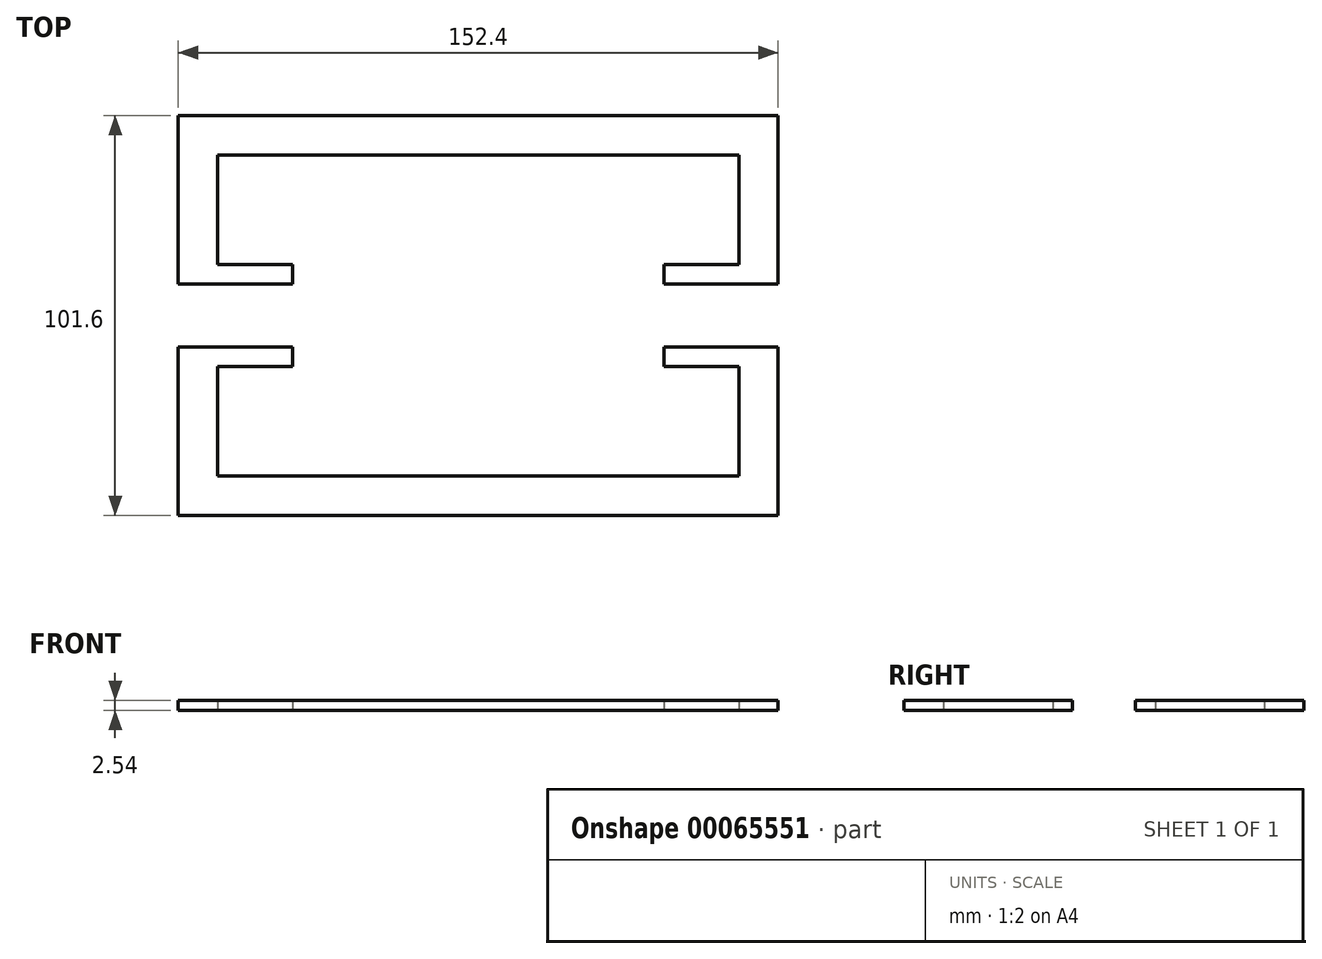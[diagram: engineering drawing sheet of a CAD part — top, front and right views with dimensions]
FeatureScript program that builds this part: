
annotation { "Feature Type Name" : "Feature", "Feature Type Description" : "" }
export const myFeature = defineFeature(function(context is Context, id is Id, definition is map)
    precondition{}
    {
        {
            var Q0;
            Q0=qCreatedBy(makeId("Top.planeOp"),FACE);
            var sketch = newSketch(context, id + "F0", { "sketchPlane" : qUnion([Q0])});
            skLineSegment(sketch, "E0", {"start": v(-76.2, 0) * mm, "end": v(76.2, 0) * mm});
            skLineSegment(sketch, "E1", {"start": v(76.2, 0) * mm, "end": v(76.2, 42.8) * mm});
            skLineSegment(sketch, "E2", {"start": v(-76.2, 0) * mm, "end": v(-76.2, 101.6) * mm});
            skLineSegment(sketch, "E3", {"start": v(76.2, 101.6) * mm, "end": v(-76.2, 101.6) * mm});
            skPoint(sketch, "E4", {"position": v(76.2, 50.8) * mm});
            skPoint(sketch, "E5", {"position": v(-76.2, 50.8) * mm});
            skPoint(sketch, "E6", {"position": v(0, 101.6) * mm});
            skPoint(sketch, "E7", {"position": v(-76.2, 58.8) * mm});
            skPoint(sketch, "E8", {"position": v(-76.2, 42.8) * mm});
            skLineSegment(sketch, "E9", {"start": v(-76.2, 58.8) * mm, "end": v(-76.2, 42.8) * mm});
            skLineSegment(sketch, "E10", {"start": v(-76.2, 58.8) * mm, "end": v(-47.2, 58.8) * mm});
            skLineSegment(sketch, "E11", {"start": v(-76.2, 42.8) * mm, "end": v(-47.2, 42.8) * mm});
            skLineSegment(sketch, "E12", {"start": v(-76.2, 37.8) * mm, "end": v(-47.2, 37.8) * mm});
            skLineSegment(sketch, "E13", {"start": v(-76.2, 63.8) * mm, "end": v(-47.2, 63.8) * mm});
            skLineSegment(sketch, "E14", {"start": v(-47.2, 63.8) * mm, "end": v(-47.2, 58.8) * mm});
            skLineSegment(sketch, "E15", {"start": v(-47.2, 42.8) * mm, "end": v(-47.2, 37.8) * mm});
            skLineSegment(sketch, "E16", {"start": v(-76.2, 63.8) * mm, "end": v(-76.2, 58.8) * mm});
            skLineSegment(sketch, "E17", {"start": v(-76.2, 42.8) * mm, "end": v(-76.2, 37.8) * mm});
            skPoint(sketch, "E18", {"position": v(76.2, 58.8) * mm});
            skPoint(sketch, "E19", {"position": v(76.2, 42.8) * mm});
            skLineSegment(sketch, "E20.trimOffspring", {"start": v(76.2, 58.8) * mm, "end": v(76.2, 101.6) * mm});
            skLineSegment(sketch, "E21", {"start": v(76.2, 42.8) * mm, "end": v(76.2, 58.8) * mm});
            skLineSegment(sketch, "E22", {"start": v(76.2, 42.8) * mm, "end": v(47.2, 42.8) * mm});
            skLineSegment(sketch, "E23", {"start": v(76.2, 37.8) * mm, "end": v(47.2, 37.8) * mm});
            skLineSegment(sketch, "E24", {"start": v(76.2, 58.8) * mm, "end": v(47.2, 58.8) * mm});
            skLineSegment(sketch, "E25", {"start": v(76.2, 63.8) * mm, "end": v(47.2, 63.8) * mm});
            skLineSegment(sketch, "E26", {"start": v(-66.2, 63.8) * mm, "end": v(-66.2, 91.6) * mm});
            skLineSegment(sketch, "E27", {"start": v(-66.2, 37.8) * mm, "end": v(-66.2, 10) * mm});
            skLineSegment(sketch, "E28", {"start": v(-66.2, 10) * mm, "end": v(66.2, 10) * mm});
            skLineSegment(sketch, "E29", {"start": v(66.2, 91.6) * mm, "end": v(66.2, 63.8) * mm});
            skLineSegment(sketch, "E30", {"start": v(66.2, 37.8) * mm, "end": v(66.2, 10) * mm});
            skLineSegment(sketch, "E31", {"start": v(-66.2, 91.6) * mm, "end": v(66.2, 91.6) * mm});
            skPoint(sketch, "E32.orphan", {"position": v(-66.2, 0) * mm});
            skPoint(sketch, "E33.orphan", {"position": v(66.2, 0) * mm});
            skLineSegment(sketch, "E34", {"start": v(47.2, 63.8) * mm, "end": v(47.2, 58.8) * mm});
            skLineSegment(sketch, "E35", {"start": v(47.2, 42.8) * mm, "end": v(47.2, 37.8) * mm});
            skSolve(sketch);
        }
        {
            var Q0;
            Q0=makeQuery(id+"F0.imprint","IMPRINT",FACE,{"disambiguationData":[TD([[makeQuery(id+"F0.imprint","IMPRINT",EDGE,{"derivedFrom":sQuery(id+"F0.wireOp",EDGE,"E10")}),1.0]])]});
            var Q1;
            Q1=makeQuery(id+"F0.imprint","IMPRINT",FACE,{"disambiguationData":[TD([[makeQuery(id+"F0.imprint","IMPRINT",EDGE,{"derivedFrom":sQuery(id+"F0.wireOp",EDGE,"E11")}),-1.0]])]});
            var Q2;
            {var subQ4=sQuery(id+"F0.wireOp",EDGE,"E0");Q2=makeQuery(id+"F0.imprint","IMPRINT",FACE,{"disambiguationData":[TD([[makeQuery(id+"F0.imprint","IMPRINT",EDGE,{"derivedFrom":subQ4}),1.0]])]});}
            var Q3;
            {var subQ3=sQuery(id+"F0.wireOp",EDGE,"E22");Q3=makeQuery(id+"F0.imprint","IMPRINT",FACE,{"disambiguationData":[TD([[makeQuery(id+"F0.imprint","IMPRINT",EDGE,{"derivedFrom":subQ3}),1.0]])]});}
            var Q4;
            {var subQ5=sQuery(id+"F0.wireOp",EDGE,"E24");Q4=makeQuery(id+"F0.imprint","IMPRINT",FACE,{"disambiguationData":[TD([[makeQuery(id+"F0.imprint","IMPRINT",EDGE,{"derivedFrom":subQ5}),-1.0]])]});}
            var Q5;
            {var subQ1=sQuery(id+"F0.wireOp",EDGE,"E3");Q5=makeQuery(id+"F0.imprint","IMPRINT",FACE,{"disambiguationData":[TD([[makeQuery(id+"F0.imprint","IMPRINT",EDGE,{"derivedFrom":subQ1}),1.0]])]});}
            var Q6;
            Q6=makeQuery(id+"F0.imprint","IMPRINT",FACE,{"disambiguationData":[TD([[makeQuery(id+"F0.imprint","IMPRINT",EDGE,{"derivedFrom":sQuery(id+"F0.wireOp",EDGE,"E9")}),1.0]])]});
            extrude(context, id + "F1", {"entities" : qUnion([Q0, Q1, Q2, Q3, Q4, Q5, Q6]), "depth" : 2.54 * mm});
        }
    });
